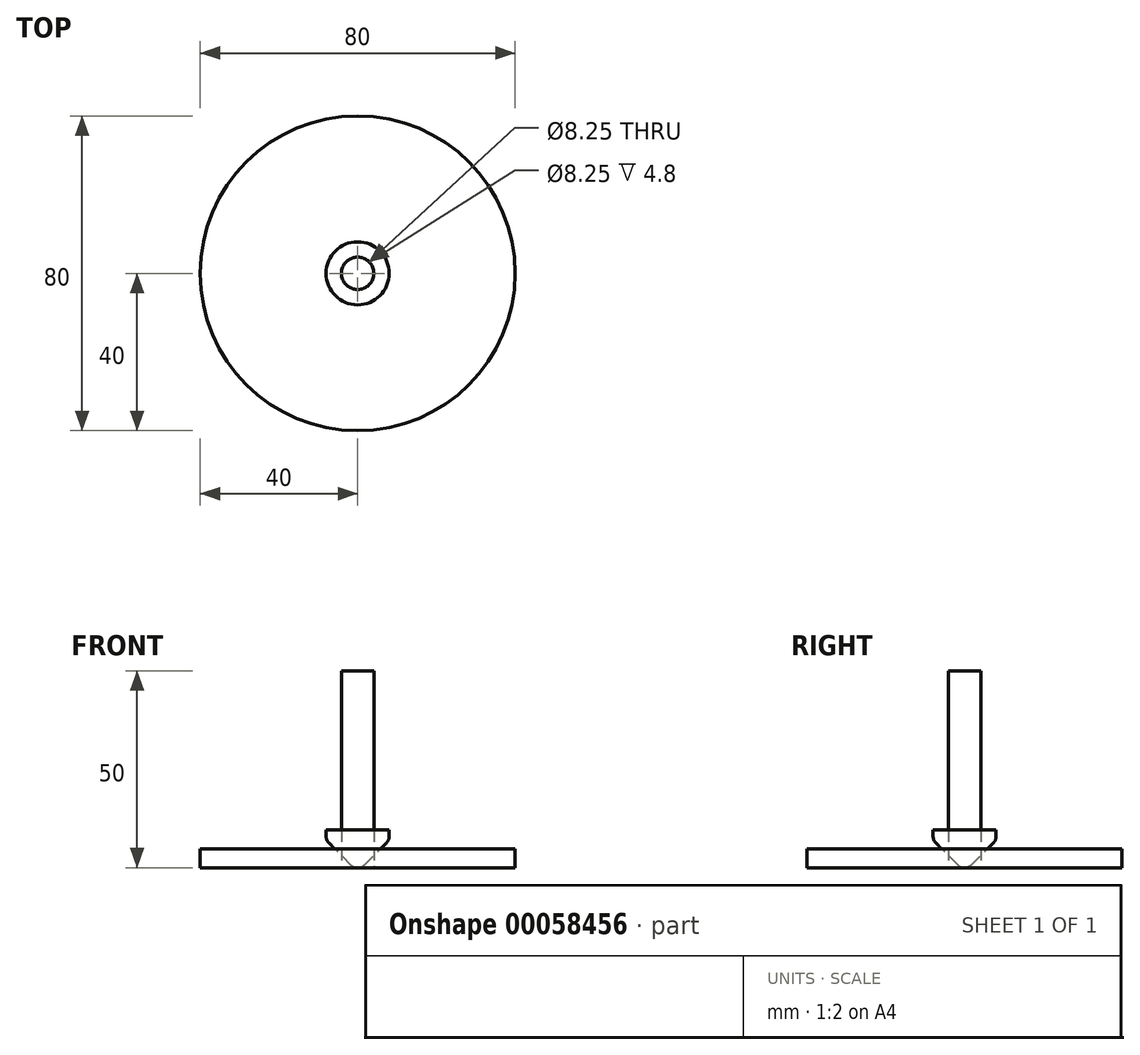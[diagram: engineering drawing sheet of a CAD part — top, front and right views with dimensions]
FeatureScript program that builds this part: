
annotation { "Feature Type Name" : "Feature", "Feature Type Description" : "" }
export const myFeature = defineFeature(function(context is Context, id is Id, definition is map)
    precondition{}
    {
        {
            assignVariable(context, id + "F0", {"name" : "MaterialThickness", "anyValue" : 4.8});
        }
        {
            assignVariable(context, id + "F1", {"name" : "Height", "anyValue" : getVariable(context, 'MaterialThickness') * 2});
        }
        {
            var Q0;
            Q0=qCreatedBy(makeId("Top.planeOp"),FACE);
            var sketch = newSketch(context, id + "F2", { "sketchPlane" : qUnion([Q0])});
            skCircle(sketch, "E0", {"center": v(0, 0) * mm, "radius": 4.12 * mm});
            skCircle(sketch, "E1", {"center": v(0, 0) * mm, "radius": 8 * mm});
            skCircle(sketch, "E2", {"center": v(0, 0) * mm, "radius": 40 * mm});
            skSolve(sketch);
        }
        {
            var Q0;
            Q0=makeQuery(id+"F2.imprint","IMPRINT",FACE,{"disambiguationData":[TD([[makeQuery(id+"F2.imprint","IMPRINT",EDGE,{"derivedFrom":sQuery(id+"F2.wireOp",EDGE,"E0")}),-1.0]])]});
            extrude(context, id + "F3", {"entities" : qUnion([Q0]), "depth" : (getVariable(context, 'Height')) * mm});
        }
        {
            var Q0;
            Q0=makeQuery(id+"F2.imprint","IMPRINT",FACE,{"disambiguationData":[TD([[makeQuery(id+"F2.imprint","IMPRINT",EDGE,{"derivedFrom":sQuery(id+"F2.wireOp",EDGE,"E0")}),1.0]])]});
            extrude(context, id + "F4", {"entities" : qUnion([Q0]), "operationType" : NewBodyOperationType.ADD, "depth" : (getVariable(context, 'Height') / 2) * mm});
        }
        {
            var Q0;
            Q0=makeQuery(id+"F3.opExtrude","CAP_EDGE",EDGE,{"disambiguationData":[OSD([sQuery(id+"F2.wireOp",EDGE,"E1")])],"isStart":true});
            chamfer(context, id + "F5", {"entities" : qUnion([Q0]), "width" : (getVariable(context, 'MaterialThickness') * 1.45) * mm, "tangentPropagation" : true});
        }
        {
            var Q0;
            {var subQ0=sQuery(id+"F2.wireOp",EDGE,"E1");Q0=makeQuery(id+"F5.opChamfer","BLEND_EDGE",EDGE,{"blendedFrom":[makeQuery(id+"F3.opExtrude","CAP_EDGE",EDGE,{"disambiguationData":[OSD([subQ0])],"isStart":true}),makeQuery(id+"F3.opExtrude","SWEPT_FACE",FACE,{"disambiguationData":[OSD([subQ0])]})],"blendedInto":[makeQuery(id+"F3.opExtrude","SWEPT_FACE",FACE,{"disambiguationData":[OSD([subQ0])]})]});}
            var Q1;
            {var subQ0=sQuery(id+"F2.wireOp",EDGE,"E0");var subQ1=sQuery(id+"F2.wireOp",EDGE,"E1");Q1=makeQuery(id+"F5.opChamfer","BLEND_EDGE",EDGE,{"blendedFrom":[makeQuery(id+"F3.opExtrude","CAP_EDGE",EDGE,{"disambiguationData":[OSD([subQ1])],"isStart":true}),makeQuery(id+"F4.boolean.opBoolean","MERGE",FACE,{"derivedFrom":[makeQuery(id+"F3.opExtrude","CAP_FACE",FACE,{"disambiguationData":[OSD([subQ0,subQ1])],"isStart":true}),makeQuery(id+"F4.opExtrude","CAP_FACE",FACE,{"disambiguationData":[OSD([subQ0])],"isStart":true})]})],"blendedInto":[makeQuery(id+"F4.boolean.opBoolean","MERGE",FACE,{"derivedFrom":[makeQuery(id+"F3.opExtrude","CAP_FACE",FACE,{"disambiguationData":[OSD([subQ0,subQ1])],"isStart":true}),makeQuery(id+"F4.opExtrude","CAP_FACE",FACE,{"disambiguationData":[OSD([subQ0])],"isStart":true})]})]});}
            fillet(context, id + "F6", {"entities" : qUnion([Q0, Q1]), "radius" : (getVariable(context, 'MaterialThickness') / 2) * mm, "allowEdgeOverflow" : false});
        }
        {
            var Q0;
            Q0=makeQuery(id+"F2.imprint","IMPRINT",FACE,{"disambiguationData":[TD([[makeQuery(id+"F2.imprint","IMPRINT",EDGE,{"derivedFrom":sQuery(id+"F2.wireOp",EDGE,"E1")}),-1.0]])]});
            var Q1;
            Q1=makeQuery(id+"F2.imprint","IMPRINT",FACE,{"disambiguationData":[TD([[makeQuery(id+"F2.imprint","IMPRINT",EDGE,{"derivedFrom":sQuery(id+"F2.wireOp",EDGE,"E0")}),-1.0]])]});
            extrude(context, id + "F7", {"entities" : qUnion([Q0, Q1]), "depth" : (getVariable(context, 'MaterialThickness')) * mm});
        }
        {
            var Q0;
            Q0=makeQuery(id+"F2.imprint","IMPRINT",FACE,{"disambiguationData":[TD([[makeQuery(id+"F2.imprint","IMPRINT",EDGE,{"derivedFrom":sQuery(id+"F2.wireOp",EDGE,"E0")}),1.0]])]});
            extrude(context, id + "F8", {"entities" : qUnion([Q0]), "depth" : 50 * mm});
        }
    });
